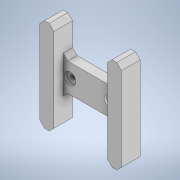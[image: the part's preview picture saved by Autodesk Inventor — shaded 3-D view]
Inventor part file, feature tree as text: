
AUTODESK INVENTOR PART (.ipt)
format: ipt  version: 2022 (Build 260153000, 153)  size: 320,000 bytes
history: native  units: mm
features: extrude x4, sketch x3, hole x1, chamfer x1
ambient origin geometry x8: Origin, YZ Plane, XZ Plane, XY Plane, X Axis, Y Axis, Z Axis, Center Point
bodies: Solid1 (feature_tree)
feature tree (9):
  sketch  "Sketch1"  dims[d0=70.0mm d1=80.0mm]
  extrude  "Extrusion1"  Depth=80.0mm
  extrude  "Extrusion2"  Depth=18.0mm
  hole  "Hole1"  [1 undecoded]
  extrude  "Extrusion3"  Depth=12.0mm
  extrude  "Extrusion4"  Depth=12.0mm
  chamfer  "Chamfer2"  Distance=6.0mm
  sketch  "Sketch2"  dims[d2=34.0mm d3=18.0mm]
  sketch  "Sketch3"  dims[d6=40.0mm d7=40.0mm d8=12.0mm d9=12.0mm d10=6.0mm d11=0.0mm d12=10.0mm d13=0.0mm d14=4.0mm d15=6.0mm d16=4.0mm d17=2.0mm d18=90.0deg d19=8.0mm d20=20.594885mm d24=24.0mm d25=28.0mm d26=6.0mm d27=0.0mm d28=10.0mm d29=10.0mm d30=2.0mm d31=0.0mm d32=4.0mm d33=2.0mm d34=45.0deg]
note: 1 required parameter value undecoded (feature->parameter linkage not recoverable at this tier; creation-order binding heuristic only, values carry confidence <= 0.55)
